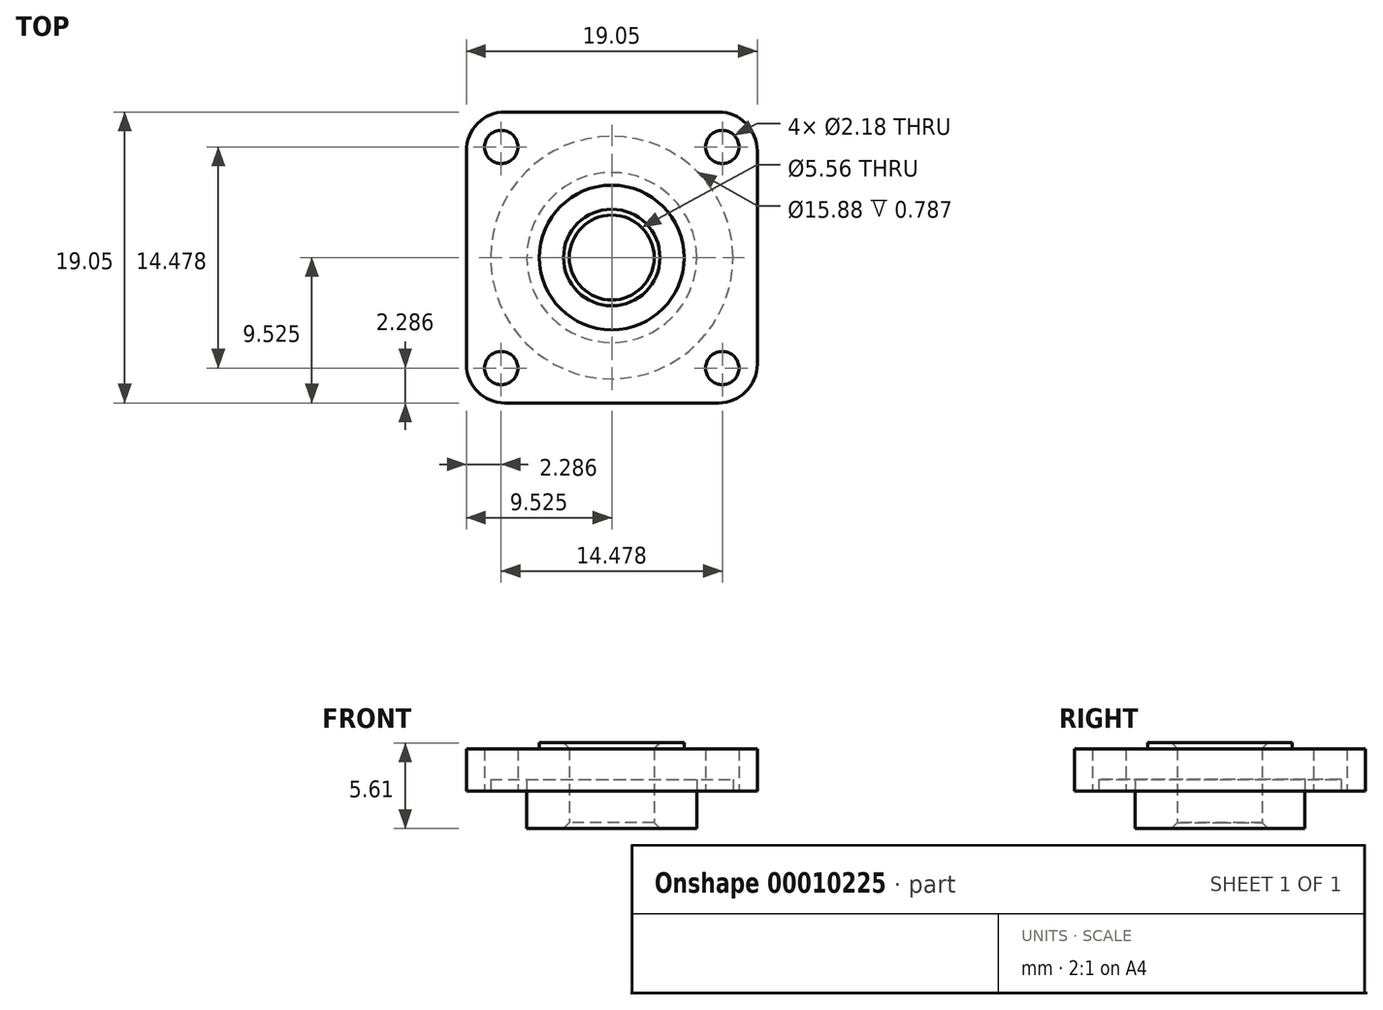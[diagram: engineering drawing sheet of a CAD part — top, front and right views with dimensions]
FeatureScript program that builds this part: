
annotation { "Feature Type Name" : "Feature", "Feature Type Description" : "" }
export const myFeature = defineFeature(function(context is Context, id is Id, definition is map)
    precondition{}
    {
        {
            var Q0;
            Q0=qCreatedBy(makeId("Top.planeOp"),FACE);
            var sketch = newSketch(context, id + "F0", { "sketchPlane" : qUnion([Q0])});
            skLineSegment(sketch, "E0.bottom", {"start": v(0, 0) * mm, "end": v(19.05, 0) * mm});
            skLineSegment(sketch, "E0.top", {"start": v(0, -19.05) * mm, "end": v(19.05, -19.05) * mm});
            skLineSegment(sketch, "E0.left", {"start": v(0, 0) * mm, "end": v(0, -19.05) * mm});
            skLineSegment(sketch, "E0.right", {"start": v(19.05, 0) * mm, "end": v(19.05, -19.05) * mm});
            skLineSegment(sketch, "E1", {"start": v(9.52, 0) * mm, "end": v(9.52, -19.05) * mm, "construction": true});
            skLineSegment(sketch, "E2", {"start": v(0, -9.53) * mm, "end": v(19.05, -9.53) * mm, "construction": true});
            skLineSegment(sketch, "E3.rect.bottom", {"start": v(16.76, -2.29) * mm, "end": v(2.29, -2.29) * mm, "construction": true});
            skLineSegment(sketch, "E3.rect.top", {"start": v(16.76, -16.76) * mm, "end": v(2.29, -16.76) * mm, "construction": true});
            skLineSegment(sketch, "E3.rect.left", {"start": v(16.76, -2.29) * mm, "end": v(16.76, -16.76) * mm, "construction": true});
            skLineSegment(sketch, "E3.rect.right", {"start": v(2.29, -2.29) * mm, "end": v(2.29, -16.76) * mm, "construction": true});
            skPoint(sketch, "E3.rect.middle", {"position": v(9.52, -9.53) * mm});
            skCircle(sketch, "E4", {"center": v(16.76, -2.29) * mm, "radius": 1.1 * mm});
            skCircle(sketch, "E5", {"center": v(2.29, -2.29) * mm, "radius": 1.1 * mm});
            skCircle(sketch, "E6", {"center": v(2.29, -16.76) * mm, "radius": 1.1 * mm});
            skCircle(sketch, "E7", {"center": v(16.76, -16.76) * mm, "radius": 1.1 * mm});
            skCircle(sketch, "E8", {"center": v(9.52, -9.53) * mm, "radius": 2.78 * mm});
            skSolve(sketch);
        }
        {
            var Q0;
            Q0 = qSketchRegion(id + "F0", true);
            extrude(context, id + "F1", {"entities" : qUnion([Q0]), "depth" : 5.2 * mm});
        }
        {
            var Q0;
            Q0=makeQuery(id+"F1.opExtrude","CAP_FACE",FACE,{"disambiguationData":[OSD([sQuery(id+"F0.wireOp",EDGE,"E0.bottom"),sQuery(id+"F0.wireOp",EDGE,"E0.top"),sQuery(id+"F0.wireOp",EDGE,"E0.left"),sQuery(id+"F0.wireOp",EDGE,"E0.right"),sQuery(id+"F0.wireOp",EDGE,"E4"),sQuery(id+"F0.wireOp",EDGE,"E5"),sQuery(id+"F0.wireOp",EDGE,"E6"),sQuery(id+"F0.wireOp",EDGE,"E7"),sQuery(id+"F0.wireOp",EDGE,"E8")])],"isStart":false});
            var sketch = newSketch(context, id + "F2", { "sketchPlane" : qUnion([Q0])});
            skCircle(sketch, "E9", {"center": v(9.52, -9.53) * mm, "radius": 4.74 * mm});
            skCircle(sketch, "E10", {"center": v(9.52, -9.53) * mm, "radius": 2.78 * mm});
            skSolve(sketch);
        }
        {
            var Q0;
            Q0 = qSketchRegion(id + "F2", true);
            extrude(context, id + "F3", {"entities" : qUnion([Q0]), "operationType" : NewBodyOperationType.ADD, "depth" : 0.4 * mm});
        }
        {
            var Q0;
            Q0=makeQuery(id+"F1.opExtrude","CAP_FACE",FACE,{"disambiguationData":[OSD([sQuery(id+"F0.wireOp",EDGE,"E0.bottom"),sQuery(id+"F0.wireOp",EDGE,"E0.top"),sQuery(id+"F0.wireOp",EDGE,"E0.left"),sQuery(id+"F0.wireOp",EDGE,"E0.right"),sQuery(id+"F0.wireOp",EDGE,"E4"),sQuery(id+"F0.wireOp",EDGE,"E5"),sQuery(id+"F0.wireOp",EDGE,"E6"),sQuery(id+"F0.wireOp",EDGE,"E7"),sQuery(id+"F0.wireOp",EDGE,"E8")])],"isStart":true});
            var sketch = newSketch(context, id + "F4", { "sketchPlane" : qUnion([Q0])});
            skCircle(sketch, "E11", {"center": v(9.52, 9.53) * mm, "radius": 5.56 * mm});
            skLineSegment(sketch, "E12.rect.bottom", {"start": v(19.05, 19.05) * mm, "end": v(0, 19.05) * mm});
            skLineSegment(sketch, "E12.rect.top", {"start": v(19.05, 0) * mm, "end": v(0, 0) * mm});
            skLineSegment(sketch, "E12.rect.left", {"start": v(19.05, 19.05) * mm, "end": v(19.05, 0) * mm});
            skLineSegment(sketch, "E12.rect.right", {"start": v(0, 19.05) * mm, "end": v(0, 0) * mm});
            skSolve(sketch);
        }
        {
            var Q0;
            Q0 = qSketchRegion(id + "F4", true);
            extrude(context, id + "F5", {"entities" : qUnion([Q0]), "operationType" : NewBodyOperationType.REMOVE, "oppositeDirection" : true, "depth" : 2.44 * mm});
        }
        {
            var Q0;
            Q0=makeQuery(id+"F5.boolean.opBoolean","COPY",FACE,{"derivedFrom":makeQuery(id+"F5.opExtrude","CAP_FACE",FACE,{"disambiguationData":[OSD([sQuery(id+"F4.wireOp",EDGE,"E11"),sQuery(id+"F4.wireOp",EDGE,"E12.rect.bottom"),sQuery(id+"F4.wireOp",EDGE,"E12.rect.top"),sQuery(id+"F4.wireOp",EDGE,"E12.rect.left"),sQuery(id+"F4.wireOp",EDGE,"E12.rect.right")])],"isStart":false})});
            var sketch = newSketch(context, id + "F6", { "sketchPlane" : qUnion([Q0])});
            skCircle(sketch, "E13", {"center": v(9.52, 9.53) * mm, "radius": 7.94 * mm});
            skCircle(sketch, "E14", {"center": v(9.52, 9.53) * mm, "radius": 5.56 * mm});
            skSolve(sketch);
        }
        {
            var Q0;
            Q0 = qSketchRegion(id + "F6", true);
            extrude(context, id + "F7", {"entities" : qUnion([Q0]), "operationType" : NewBodyOperationType.REMOVE, "oppositeDirection" : true, "depth" : 0.79 * mm});
        }
        {
            var Q0;
            Q0=makeQuery(id+"F3.boolean.opBoolean","MERGE",FACE,{"derivedFrom":[makeQuery(id+"F1.opExtrude","SWEPT_FACE",FACE,{"disambiguationData":[OSD([sQuery(id+"F0.wireOp",EDGE,"E8")])]}),makeQuery(id+"F3.opExtrude","SWEPT_FACE",FACE,{"disambiguationData":[OSD([sQuery(id+"F2.wireOp",EDGE,"E10")])]})]});
            chamfer(context, id + "F8", {"entities" : qUnion([Q0]), "width" : 0.38 * mm, "tangentPropagation" : true});
        }
        {
            var Q0;
            Q0=makeQuery(id+"F1.opExtrude","SWEPT_EDGE",EDGE,{"disambiguationData":[OSD([sQuery(id+"F0.wireOp",EDGE,"E0.bottom"),sQuery(id+"F0.wireOp",EDGE,"E0.left")])]});
            var Q1;
            Q1=makeQuery(id+"F1.opExtrude","SWEPT_EDGE",EDGE,{"disambiguationData":[OSD([sQuery(id+"F0.wireOp",EDGE,"E0.bottom"),sQuery(id+"F0.wireOp",EDGE,"E0.right")])]});
            var Q2;
            Q2=makeQuery(id+"F1.opExtrude","SWEPT_EDGE",EDGE,{"disambiguationData":[OSD([sQuery(id+"F0.wireOp",EDGE,"E0.top"),sQuery(id+"F0.wireOp",EDGE,"E0.right")])]});
            var Q3;
            Q3=makeQuery(id+"F1.opExtrude","SWEPT_EDGE",EDGE,{"disambiguationData":[OSD([sQuery(id+"F0.wireOp",EDGE,"E0.top"),sQuery(id+"F0.wireOp",EDGE,"E0.left")])]});
            fillet(context, id + "F9", {"entities" : qUnion([Q0, Q1, Q2, Q3]), "radius" : 2.54 * mm, "tangentPropagation" : true, "allowEdgeOverflow" : false});
        }
    });
